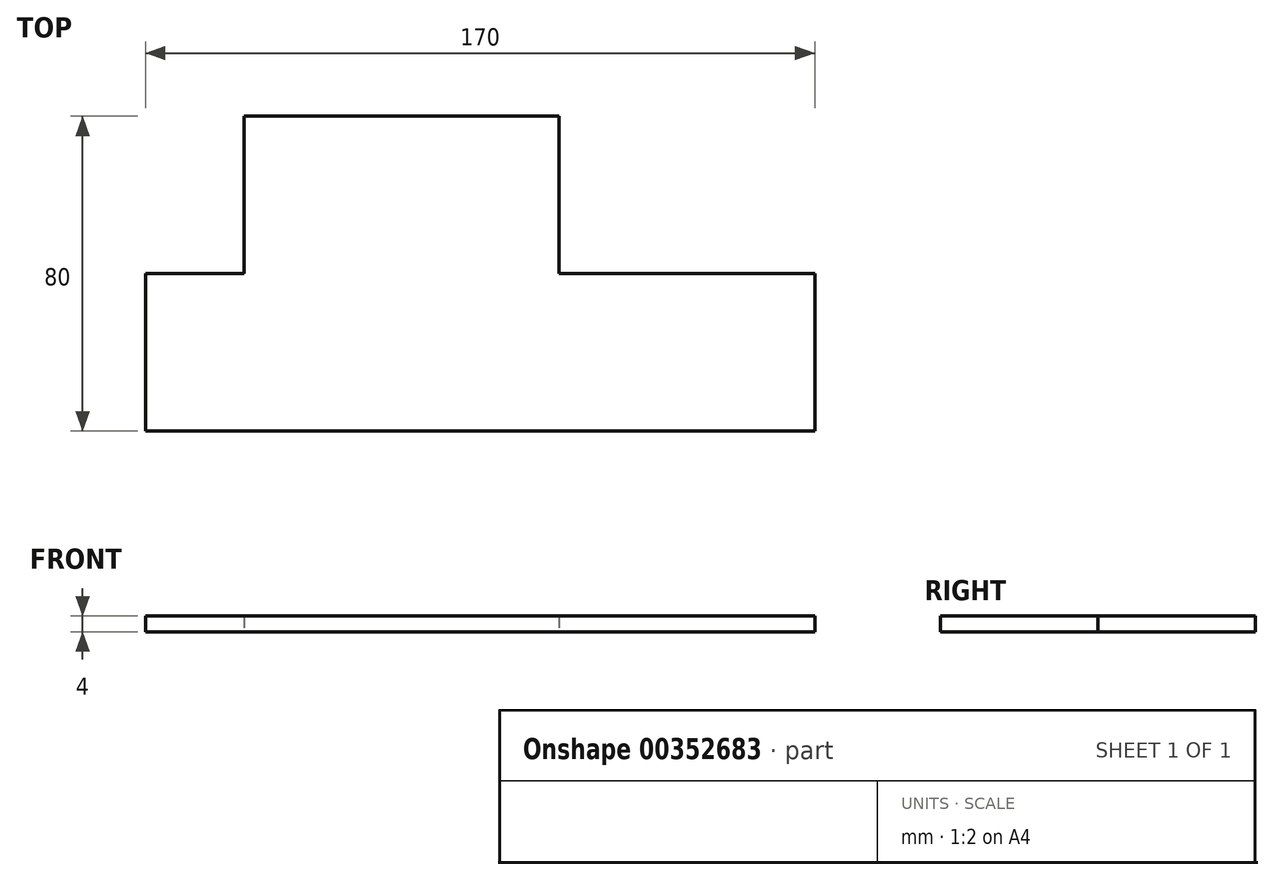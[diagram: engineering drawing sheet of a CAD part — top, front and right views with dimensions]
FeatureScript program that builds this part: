
annotation { "Feature Type Name" : "Feature", "Feature Type Description" : "" }
export const myFeature = defineFeature(function(context is Context, id is Id, definition is map)
    precondition{}
    {
        {
            var Q0;
            Q0=qCreatedBy(makeId("Top.planeOp"),FACE);
            var sketch = newSketch(context, id + "F0", { "sketchPlane" : qUnion([Q0])});
            skLineSegment(sketch, "E0.bottom", {"start": v(-60, 40) * mm, "end": v(20, 40) * mm});
            skLineSegment(sketch, "E0.top", {"start": v(-85, -40) * mm, "end": v(85, -40) * mm});
            skLineSegment(sketch, "E0.left", {"start": v(-85, 0) * mm, "end": v(-85, -40) * mm});
            skLineSegment(sketch, "E0.right", {"start": v(85, 0) * mm, "end": v(85, -40) * mm});
            skPoint(sketch, "E0.middle", {"position": v(0, 0) * mm});
            skLineSegment(sketch, "E1", {"start": v(-60, 40) * mm, "end": v(-60, 0) * mm});
            skLineSegment(sketch, "E2", {"start": v(20, 40) * mm, "end": v(20, 0) * mm});
            skLineSegment(sketch, "E3", {"start": v(-60, 0) * mm, "end": v(-85, 0) * mm});
            skLineSegment(sketch, "E4", {"start": v(20, 0) * mm, "end": v(85, 0) * mm});
            skSolve(sketch);
        }
        {
            var Q0;
            Q0 = qSketchRegion(id + "F0", true);
            extrude(context, id + "F1", {"entities" : qUnion([Q0]), "depth" : 4 * mm});
        }
    });
